# Revit family: Faucet-Deck_Mounted-Waterworks-Flyte-One_Hole
name_source: partatom
category: Plumbing Fixtures
revit_build: Autodesk Revit MEP 2014 (Build: 20140709_2115(x64)
units: mm (PartAtom-declared; Revit-internal decimal feet)

## types (4) — shared parameters
ADA Compliant = Yes
Anti-scald Protection = No
Assembly Code = D2010
CW Connection = Yes
Certification CEC = Yes
Certification IAPMO = Yes
Certification NSF = Yes
Certification State of MA = Yes
Certification Watersense = Yes
Certification cUPC = Yes
Code Compliance = Code # FLLS50: CEC, Watersense
Cold Water Connector = Cold Water - Compression Connector Hose
Cold Water Diameter = 0' - 0 3/8"
Default Elevation = 2' - 10"
Depth = 0' - 7 5/8"
Domestic Water Flow Rate = 1 GPM
Fittings Hole Diameter = 0' - 1 3/8"
HW Connection = Yes
Height = 0' - 5 7/8"
Hot Limit Safety Stop = No
Hot Water Connector = Hot Water - Compression Connector Hose
Hot Water Diameter = 0' - 0 3/8"
Keynote = 22 40 00
Length = 1' - 3 1/4"
Manufacturer = Waterworks
Model = FLLS50
Pressure = 45.00 psi
Product Documentation Link = http://assets.waterworks.com
Product Name = Flyte Low Profile Three Hole Deck Mounted Lavatory Faucet with Metal Cross Handles
Product Page URL = http://www.waterworks.com
Spout Reach = 0' - 6"
URL = http://www.waterworks.com
Valve Material = Ceramic
Vent Connection = No
Version = 2014 - v1.0a
Warranty = http://www.waterworks.com
Waste Connection = No
Water Pressure = Max: 85psi / Min: 20psi / Recommended: 45psi
‌Installation Requirements or Notes = Standard flow rate is 1.2gpm (4.5 L/min)
zero-valued in all types: CWFU, HWFU, WFU

## per-type parameters (varying)
| type | ControlM | Description | Finish | Model SKU |
| 1.2gpm - Chrome | 1 | 1.2gpm 1-Hole Deck Mounted Faucet Fixed Spray, Lever Handles in with Chrome Lever | Metal - Waterworks - Chrome | 07-55100-72476 |
| 1.2gpm - Graphite | 3 | 1.2gpm 1-Hole Deck Mounted Faucet Fixed Spray, Lever Handles in with Graphite Lever | Metal - Waterworks - Graphite | 07-13199-02491 |
| 1.2gpm - Nickel | 4 | 1.2gpm 1-Hole Deck Mounted Faucet Fixed Spray, Lever Handles in with Nickel Lever | Metal - Waterworks - Nickel | 07-78139-07177 |
| 1.2gpm - Unlacquered Brass | 6 | 1.2gpm 1-Hole Deck Mounted Faucet Fixed Spray, Lever Handles in with Unlacquered Brass Lever | Metal - Waterworks - Unlacquered Brass | 07-34566-02036 |

## geometry (parser evidence)
native form markers: Sweep x6
no freeform markers — native parametric forms only
